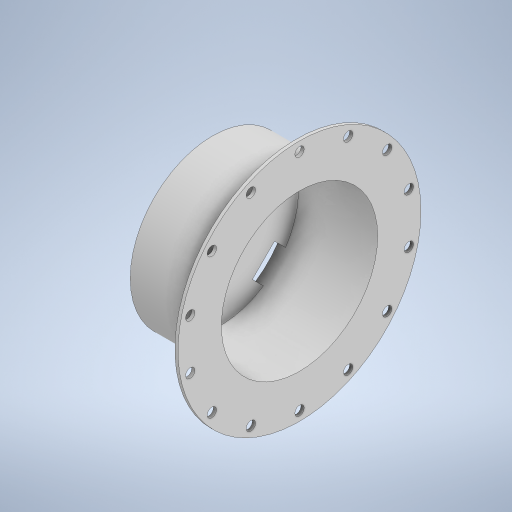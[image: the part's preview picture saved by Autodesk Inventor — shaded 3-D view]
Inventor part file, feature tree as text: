
AUTODESK INVENTOR PART (.ipt)
format: ipt  version: 2023 (Build 270158000, 158)  size: 342,016 bytes
history: native  units: mm
features: extrude x4, sketch x3
ambient origin geometry x8: Origin, YZ Plane, XZ Plane, XY Plane, X Axis, Y Axis, Z Axis, Center Point
bodies: Solid1 (feature_tree)
feature tree (7):
  extrude  "Extrusion1"  Depth=3.5mm
  extrude  "Extrusion2"  Depth=105.0mm
  extrude  "Extrusion4"  Depth=5.0mm TaperAngle=0.0deg
  extrude  "Extrusion6"  Depth=2.0mm
  sketch  "Sketch1"  dims[d0=38.0mm d1=3.5mm]
  sketch  "Sketch2"  dims[d2=40.0mm d4=360.0deg d6=105.0mm]
  sketch  "Sketch6"  dims[d7=80.0mm d8=5.0mm d9=0.0mm d10=105.0mm d11=53.5mm d12=0.0mm d27=30.0mm d28=10.0mm d29=45.0deg d30=10.0mm d31=10.0mm d32=0.0mm d34=10.0mm d35=143.0mm d36=6.0mm d37=70.0mm d39=360.0deg d41=155.0mm d44=140.0mm d46=360.0deg d48=2.0mm d49=0.0mm]
